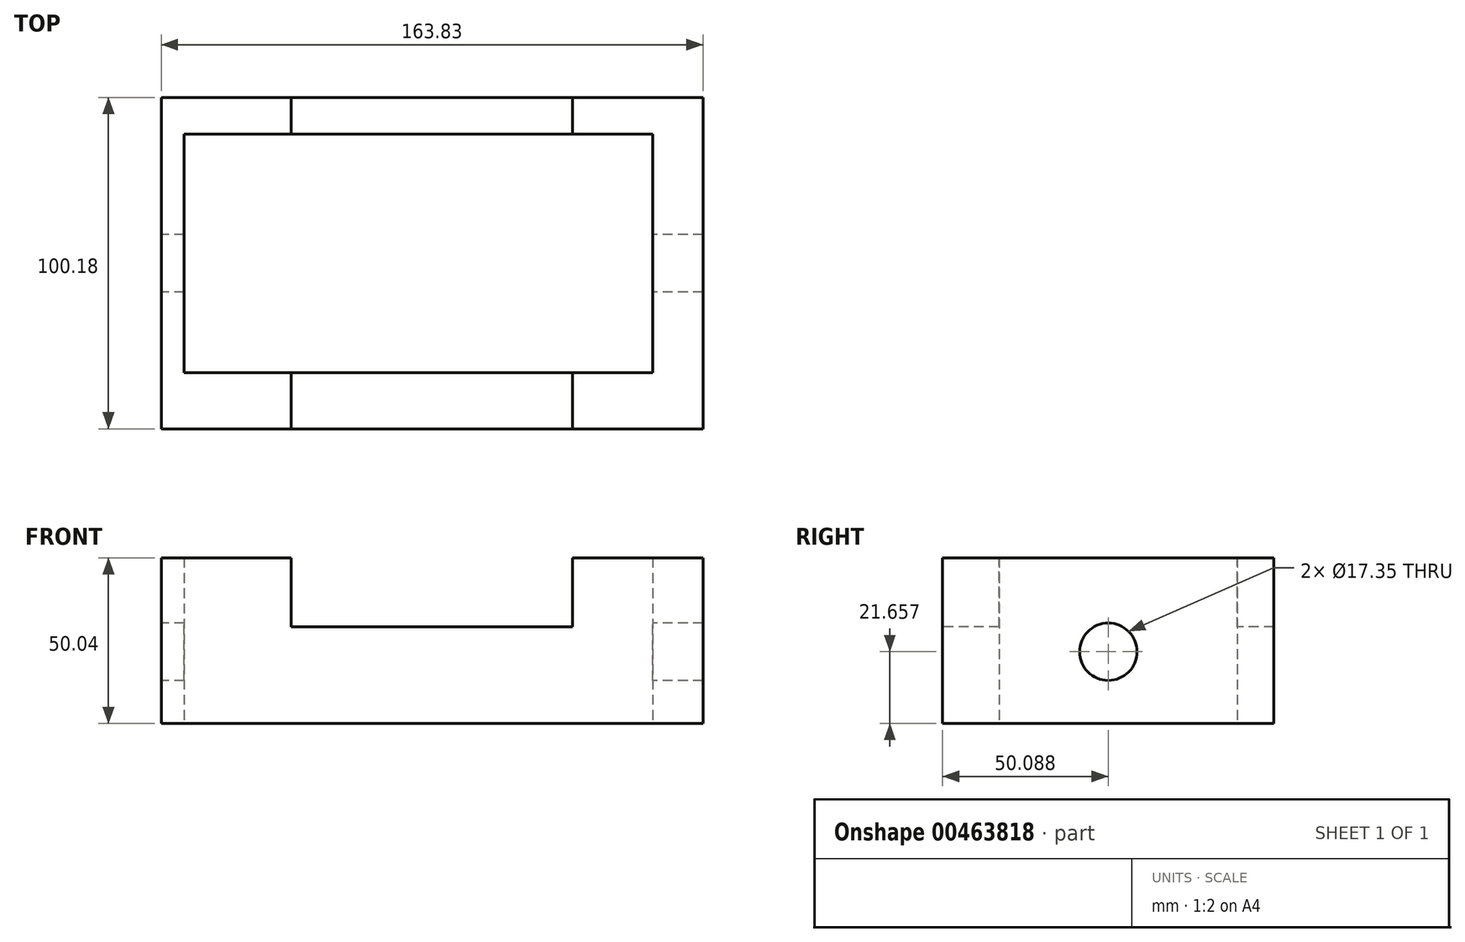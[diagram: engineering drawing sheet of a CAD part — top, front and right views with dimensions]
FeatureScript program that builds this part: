
annotation { "Feature Type Name" : "Feature", "Feature Type Description" : "" }
export const myFeature = defineFeature(function(context is Context, id is Id, definition is map)
    precondition{}
    {
        {
            var Q0;
            Q0=qCreatedBy(makeId("Top.planeOp"),FACE);
            var sketch = newSketch(context, id + "F0", { "sketchPlane" : qUnion([Q0])});
            skLineSegment(sketch, "E0.bottom", {"start": v(-71.54, 37.25) * mm, "end": v(92.29, 37.25) * mm});
            skLineSegment(sketch, "E0.top", {"start": v(-71.54, -62.93) * mm, "end": v(92.29, -62.93) * mm});
            skLineSegment(sketch, "E0.left", {"start": v(-71.54, 37.25) * mm, "end": v(-71.54, -62.93) * mm});
            skLineSegment(sketch, "E0.right", {"start": v(92.29, 37.25) * mm, "end": v(92.29, -62.93) * mm});
            skLineSegment(sketch, "E1.bottom", {"start": v(-64.61, 26.18) * mm, "end": v(77.07, 26.18) * mm});
            skLineSegment(sketch, "E1.top", {"start": v(-64.61, -45.9) * mm, "end": v(77.07, -45.9) * mm});
            skLineSegment(sketch, "E1.left", {"start": v(-64.61, 26.18) * mm, "end": v(-64.61, -45.9) * mm});
            skLineSegment(sketch, "E1.right", {"start": v(77.07, 26.18) * mm, "end": v(77.07, -45.9) * mm});
            skSolve(sketch);
        }
        {
            var Q0;
            Q0=makeQuery(id+"F0.imprint","IMPRINT",FACE,{"disambiguationData":[TD([[makeQuery(id+"F0.imprint","IMPRINT",EDGE,{"derivedFrom":sQuery(id+"F0.wireOp",EDGE,"E0.bottom")}),-1.0]])]});
            extrude(context, id + "F1", {"entities" : qUnion([Q0]), "depth" : 50.04 * mm});
        }
        {
            var Q0;
            Q0=makeQuery(id+"F1.opExtrude","SWEPT_FACE",FACE,{"disambiguationData":[OSD([sQuery(id+"F0.wireOp",EDGE,"E0.top")])]});
            var sketch = newSketch(context, id + "F2", { "sketchPlane" : qUnion([Q0])});
            skLineSegment(sketch, "E2.bottom", {"start": v(-32.26, 64.07) * mm, "end": v(52.86, 64.07) * mm});
            skLineSegment(sketch, "E2.top", {"start": v(-32.26, 29.18) * mm, "end": v(52.86, 29.18) * mm});
            skLineSegment(sketch, "E2.left", {"start": v(-32.26, 64.07) * mm, "end": v(-32.26, 29.18) * mm});
            skLineSegment(sketch, "E2.right", {"start": v(52.86, 64.07) * mm, "end": v(52.86, 29.18) * mm});
            skSolve(sketch);
        }
        {
            var Q0;
            {var subQ0=sQuery(id+"F2.wireOp",EDGE,"E2.top");Q0=makeQuery(id+"F2.imprint","IMPRINT",FACE,{"disambiguationData":[TD([[makeQuery(id+"F2.imprint","IMPRINT",EDGE,{"derivedFrom":subQ0}),1.0]])]});}
            extrude(context, id + "F3", {"entities" : qUnion([Q0]), "operationType" : NewBodyOperationType.REMOVE, "oppositeDirection" : true, "depth" : 132.84 * mm});
        }
        {
            var Q0;
            Q0=makeQuery(id+"F1.opExtrude","SWEPT_FACE",FACE,{"disambiguationData":[OSD([sQuery(id+"F0.wireOp",EDGE,"E0.left")])]});
            var sketch = newSketch(context, id + "F4", { "sketchPlane" : qUnion([Q0])});
            skCircle(sketch, "E3", {"center": v(12.84, 21.66) * mm, "radius": 8.67 * mm});
            skPoint(sketch, "E3.centerSnap0", {"position": v(12.84, 50.04) * mm});
            skSolve(sketch);
        }
        {
            var Q0;
            Q0=makeQuery(id+"F4.imprint","IMPRINT",FACE,{"disambiguationData":[TD([[makeQuery(id+"F4.imprint","IMPRINT",EDGE,{"derivedFrom":sQuery(id+"F4.wireOp",EDGE,"E3")}),1.0]])]});
            extrude(context, id + "F5", {"entities" : qUnion([Q0]), "operationType" : NewBodyOperationType.REMOVE, "oppositeDirection" : true, "depth" : 191.52 * mm});
        }
    });
